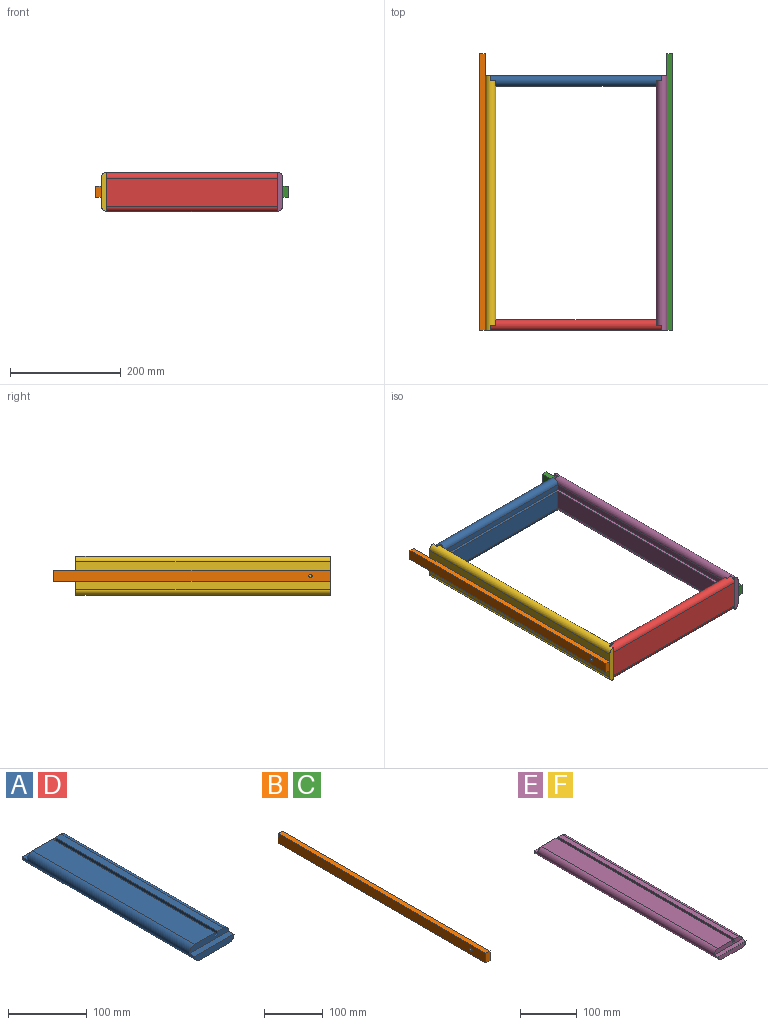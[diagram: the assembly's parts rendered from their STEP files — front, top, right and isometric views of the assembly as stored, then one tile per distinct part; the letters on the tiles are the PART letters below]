
ASSEMBLY  parts=6 mates=5
PART A: 14 faces, bbox 70x309.6x19 mm
  f0: plane 290.6x10mm, normal (0,0,1), area 2906mm2, adj f2,f7,f11,f13
  f1: plane 290.6x36mm, normal (0,0,1), area 10461.6mm2, adj f3,f6,f11,f13
  f2: plane 290.6x5mm, normal (-1,0,0), area 1453mm2, adj f0,f4,f11,f13
  f3: plane 290.6x5mm, normal (1,0,0), area 1453mm2, adj f1,f4,f11,f13
  f4: plane 290.6x5mm, normal (0,0,1), area 1453mm2, adj f2,f3,f11,f13
  f5: plane 70x9.5mm, normal (0,-1,0), area 626.3mm2, adj f6,f7,f9,f12
  f6: cylinder r=9.5mm len=309.6mm, axis (0,1,0), area 8956.5mm2, adj f1,f5,f8,f9,f10,f11,f12,f13
  f7: cylinder r=9.5mm len=309.6mm, axis (0,1,0), area 8956.5mm2, adj f0,f5,f8,f9,f10,f11,f12,f13
  f8: plane 70x9.5mm, normal (0,1,0), area 626.3mm2, adj f6,f7,f9,f10
  f9: plane 309.6x51mm, normal (0,0,-1), area 15789.6mm2, adj f5,f6,f7,f8
  f10: plane 70x9.5mm, normal (0,0,1), area 665mm2, adj f6,f7,f8,f11
  f11: plane 70x9.5mm, normal (0,1,0), area 601.3mm2, adj f0,f1,f2,f3,f4,f6,f7,f10
  f12: plane 70x9.5mm, normal (0,0,1), area 665mm2, adj f5,f6,f7,f13
  f13: plane 70x9.5mm, normal (0,-1,0), area 601.3mm2, adj f0,f1,f2,f3,f4,f6,f7,f12
PART B: 7 faces, bbox 10x500x20 mm
  f0: plane 500x20mm, normal (-1,0,0), area 9971.7mm2, adj f1,f3,f4,f5,f6
  f1: plane 20x10mm, normal (0,1,0), area 200mm2, adj f0,f2,f4,f5
  f2: plane 500x20mm, normal (1,0,0), area 9971.7mm2, adj f1,f3,f4,f5,f6
  f3: plane 20x10mm, normal (0,-1,0), area 200mm2, adj f0,f2,f4,f5
  f4: plane 500x10mm, normal (0,0,-1), area 5000mm2, adj f0,f1,f2,f3
  f5: plane 500x10mm, normal (0,0,1), area 5000mm2, adj f0,f1,f2,f3
  f6: cylinder r=3mm len=10mm, axis (-1,0,0), area 188.5mm2, adj f0,f2
PART C: same geometry as B
PART D: same geometry as A
PART E: 14 faces, bbox 70x460x19 mm
  f0: plane 441x36mm, normal (0,0,1), area 15876mm2, adj f3,f8,f10,f13
  f1: plane 441x10mm, normal (0,0,1), area 4410mm2, adj f2,f6,f10,f13
  f2: plane 441x5mm, normal (-1,0,0), area 2205mm2, adj f1,f4,f10,f13
  f3: plane 441x5mm, normal (1,0,0), area 2205mm2, adj f0,f4,f10,f13
  f4: plane 441x5mm, normal (0,0,1), area 2205mm2, adj f2,f3,f10,f13
  f5: plane 70x9.5mm, normal (0,1,0), area 626.3mm2, adj f6,f8,f9,f12
  f6: cylinder r=9.5mm len=460mm, axis (0,1,0), area 13445.2mm2, adj f1,f5,f7,f9,f10,f11,f12,f13
  f7: plane 70x9.5mm, normal (0,-1,0), area 626.3mm2, adj f6,f8,f9,f11
  f8: cylinder r=9.5mm len=460mm, axis (0,1,0), area 13445.2mm2, adj f0,f5,f7,f9,f10,f11,f12,f13
  f9: plane 460x51mm, normal (0,0,-1), area 23460mm2, adj f5,f6,f7,f8
  f10: plane 70x9.5mm, normal (0,-1,0), area 601.3mm2, adj f0,f1,f2,f3,f4,f6,f8,f11
  f11: plane 70x9.5mm, normal (0,0,1), area 665mm2, adj f6,f7,f8,f10
  f12: plane 70x9.5mm, normal (0,0,1), area 665mm2, adj f5,f6,f8,f13
  f13: plane 70x9.5mm, normal (0,1,0), area 601.3mm2, adj f0,f1,f2,f3,f4,f6,f8,f12
PART F: same geometry as E
PLACE A rot(axis=(0.58,-0.58,0.58),120deg) t=(1030.14,80.75,-522.71)mm
PLACE B t=(652.16,100.24,-890.4)mm
PLACE C t=(990.24,100.24,-890.4)mm
PLACE D rot(axis=(-0.58,-0.58,-0.58),120deg) t=(1340,-470.11,-523.25)mm
PLACE E rot(axis=(0,-1,0),90deg) t=(1349.24,35.24,-522.54)mm
PLACE F rot(axis=(-0.71,0,-0.71),180deg) t=(1021.16,-424.76,-522.54)mm
MATE fastened B.f3 <-> F.f5  axis (0,-1,0) through (1021.16,-424.76,-557.54)mm
MATE fastened C.f3 <-> E.f7  axis (0,-1,0) through (1349.24,-424.76,-557.54)mm
MATE fastened D.f12 <-> F.f13  axis (0,1,0) through (1035.15,-415.26,-558.08)mm
MATE fastened E.f12 <-> A.f5  axis (-1,0,0) through (1339.74,30.49,-557.54)mm
MATE fastened E.f10 <-> D.f10  axis (0,-1,0) through (1335.25,-415.26,-558.08)mm
